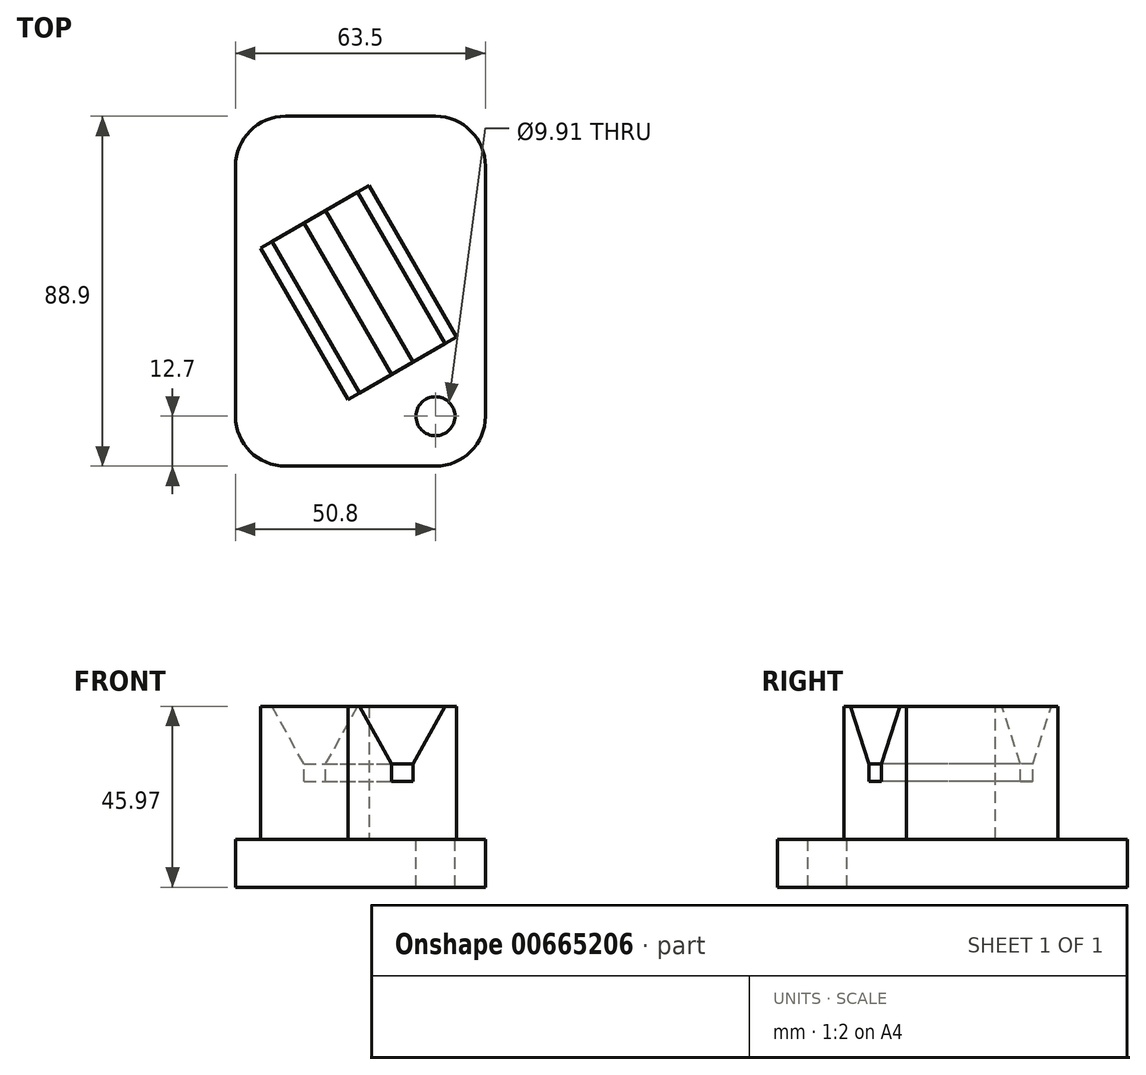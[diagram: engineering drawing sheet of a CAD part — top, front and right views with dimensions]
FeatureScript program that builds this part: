
annotation { "Feature Type Name" : "Feature", "Feature Type Description" : "" }
export const myFeature = defineFeature(function(context is Context, id is Id, definition is map)
    precondition{}
    {
        {
            var Q0;
            Q0=qCreatedBy(makeId("Top.planeOp"),FACE);
            var sketch = newSketch(context, id + "F0", { "sketchPlane" : qUnion([Q0])});
            skLineSegment(sketch, "E0.bottom", {"start": v(31.75, -44.45) * mm, "end": v(-31.75, -44.45) * mm});
            skLineSegment(sketch, "E0.top", {"start": v(31.75, 44.45) * mm, "end": v(-31.75, 44.45) * mm});
            skLineSegment(sketch, "E0.left", {"start": v(31.75, -44.45) * mm, "end": v(31.75, 44.45) * mm});
            skLineSegment(sketch, "E0.right", {"start": v(-31.75, -44.45) * mm, "end": v(-31.75, 44.45) * mm});
            skPoint(sketch, "E0.middle", {"position": v(0, 0) * mm});
            skPoint(sketch, "E1", {"position": v(19.05, -31.75) * mm});
            skSolve(sketch);
        }
        {
            var Q0;
            Q0 = qSketchRegion(id + "F0", true);
            extrude(context, id + "F1", {"entities" : qUnion([Q0]), "oppositeDirection" : true, "depth" : 12.2 * mm, "offsetDistance" : 25.4 * mm});
        }
        {
            var Q0;
            Q0=sQuery(id+"F0.wireOp",VERTEX,"E1");
            var Q1;
            Q1=makeQuery(id+"F1.opExtrude","SWEPT_BODY",BODY,{"disambiguationData":[OSD([sQuery(id+"F0.wireOp",EDGE,"E0.bottom"),sQuery(id+"F0.wireOp",EDGE,"E0.top"),sQuery(id+"F0.wireOp",EDGE,"E0.left"),sQuery(id+"F0.wireOp",EDGE,"E0.right")])]});
            hole(context, id + "F2", {"style" : HoleStyle.SIMPLE, "endStyle" : HoleEndStyle.THROUGH, "holeDiameter" : 9.9 * mm, "majorDiameter" : 6.35 * mm, "isTappedThrough" : true, "tappedDepth" : 12.7 * mm, "tapClearance" : 3, "locations" : qUnion([Q0]), "scope" : qUnion([Q1])});
        }
        {
            var Q0;
            Q0=makeQuery(id+"F0.imprint","IMPRINT",FACE,{"disambiguationData":[TD([[makeQuery(id+"F0.imprint","IMPRINT",EDGE,{"derivedFrom":sQuery(id+"F0.wireOp",EDGE,"E0.bottom")}),-1.0]])]});
            var sketch = newSketch(context, id + "F3", { "sketchPlane" : qUnion([Q0])});
            skLineSegment(sketch, "E2", {"start": v(24.38, -11.68) * mm, "end": v(2.16, 26.81) * mm});
            skLineSegment(sketch, "E3", {"start": v(2.16, 26.81) * mm, "end": v(-25.34, 10.94) * mm});
            skLineSegment(sketch, "E4", {"start": v(-25.34, 10.94) * mm, "end": v(-3.11, -27.56) * mm});
            skLineSegment(sketch, "E5", {"start": v(-3.11, -27.56) * mm, "end": v(24.38, -11.68) * mm});
            skSolve(sketch);
        }
        {
            var Q0;
            Q0=sQuery(id+"F3.wireOp",VERTEX,"E5.start");
            var Q1;
            Q1=sQuery(id+"F3.wireOp",EDGE,"E4");
            cPlane(context, id + "F4", {"entities" : qUnion([Q0, Q1]), "cplaneType" : CPlaneType.LINE_POINT, "offset" : 25.4 * mm, "width" : 152.4 * mm, "height" : 152.4 * mm});
        }
        {
            var Q0;
            Q0=qCreatedBy(id+"F4.planeOp",FACE);
            var sketch = newSketch(context, id + "F5", { "sketchPlane" : qUnion([Q0])});
            skLineSegment(sketch, "E6.0", {"start": v(-16.47, 0) * mm, "end": v(15.28, 0) * mm});
            skLineSegment(sketch, "E7", {"start": v(-16.47, 0) * mm, "end": v(-16.47, 33.78) * mm});
            skLineSegment(sketch, "E8", {"start": v(-16.47, 33.78) * mm, "end": v(-13.17, 33.78) * mm});
            skLineSegment(sketch, "E9", {"start": v(-3.77, 14.73) * mm, "end": v(2.58, 14.73) * mm});
            skLineSegment(sketch, "E10", {"start": v(11.97, 33.78) * mm, "end": v(15.28, 33.78) * mm});
            skLineSegment(sketch, "E11", {"start": v(15.28, 33.78) * mm, "end": v(15.28, 0) * mm});
            skLineSegment(sketch, "E12", {"start": v(-0.6, 14.73) * mm, "end": v(-0.6, 0) * mm, "construction": true});
            skLineSegment(sketch, "E13", {"start": v(2.58, 14.73) * mm, "end": v(2.58, 19.08) * mm});
            skLineSegment(sketch, "E14", {"start": v(2.58, 19.08) * mm, "end": v(11.97, 33.78) * mm});
            skLineSegment(sketch, "E15", {"start": v(-3.77, 14.73) * mm, "end": v(-3.77, 19.08) * mm});
            skLineSegment(sketch, "E16", {"start": v(-3.77, 19.08) * mm, "end": v(-13.17, 33.78) * mm});
            skSolve(sketch);
        }
        {
            var Q0;
            Q0=makeQuery(id+"F5.imprint","IMPRINT",FACE,{"disambiguationData":[TD([[makeQuery(id+"F5.imprint","IMPRINT",EDGE,{"derivedFrom":sQuery(id+"F5.wireOp",EDGE,"E6.0")}),1.0]])]});
            var Q1;
            Q1=sQuery(id+"F3.wireOp",VERTEX,"E4.start");
            extrude(context, id + "F6", {"entities" : qUnion([Q0]), "operationType" : NewBodyOperationType.ADD, "endBound" : BoundingType.UP_TO_VERTEX, "oppositeDirection" : true, "depth" : 21.59 * mm, "endBoundEntityVertex" : qUnion([Q1]), "offsetDistance" : 25.4 * mm});
        }
        {
            var Q0;
            Q0=makeQuery(id+"F1.opExtrude","SWEPT_EDGE",EDGE,{"disambiguationData":[OSD([sQuery(id+"F0.wireOp",EDGE,"E0.bottom"),sQuery(id+"F0.wireOp",EDGE,"E0.left")])]});
            var Q1;
            Q1=makeQuery(id+"F1.opExtrude","SWEPT_EDGE",EDGE,{"disambiguationData":[OSD([sQuery(id+"F0.wireOp",EDGE,"E0.top"),sQuery(id+"F0.wireOp",EDGE,"E0.left")])]});
            var Q2;
            Q2=makeQuery(id+"F1.opExtrude","SWEPT_EDGE",EDGE,{"disambiguationData":[OSD([sQuery(id+"F0.wireOp",EDGE,"E0.top"),sQuery(id+"F0.wireOp",EDGE,"E0.right")])]});
            var Q3;
            Q3=makeQuery(id+"F1.opExtrude","SWEPT_EDGE",EDGE,{"disambiguationData":[OSD([sQuery(id+"F0.wireOp",EDGE,"E0.bottom"),sQuery(id+"F0.wireOp",EDGE,"E0.right")])]});
            fillet(context, id + "F7", {"entities" : qUnion([Q0, Q1, Q2, Q3]), "radius" : 12.7 * mm, "tangentPropagation" : true, "allowEdgeOverflow" : false});
        }
    });
